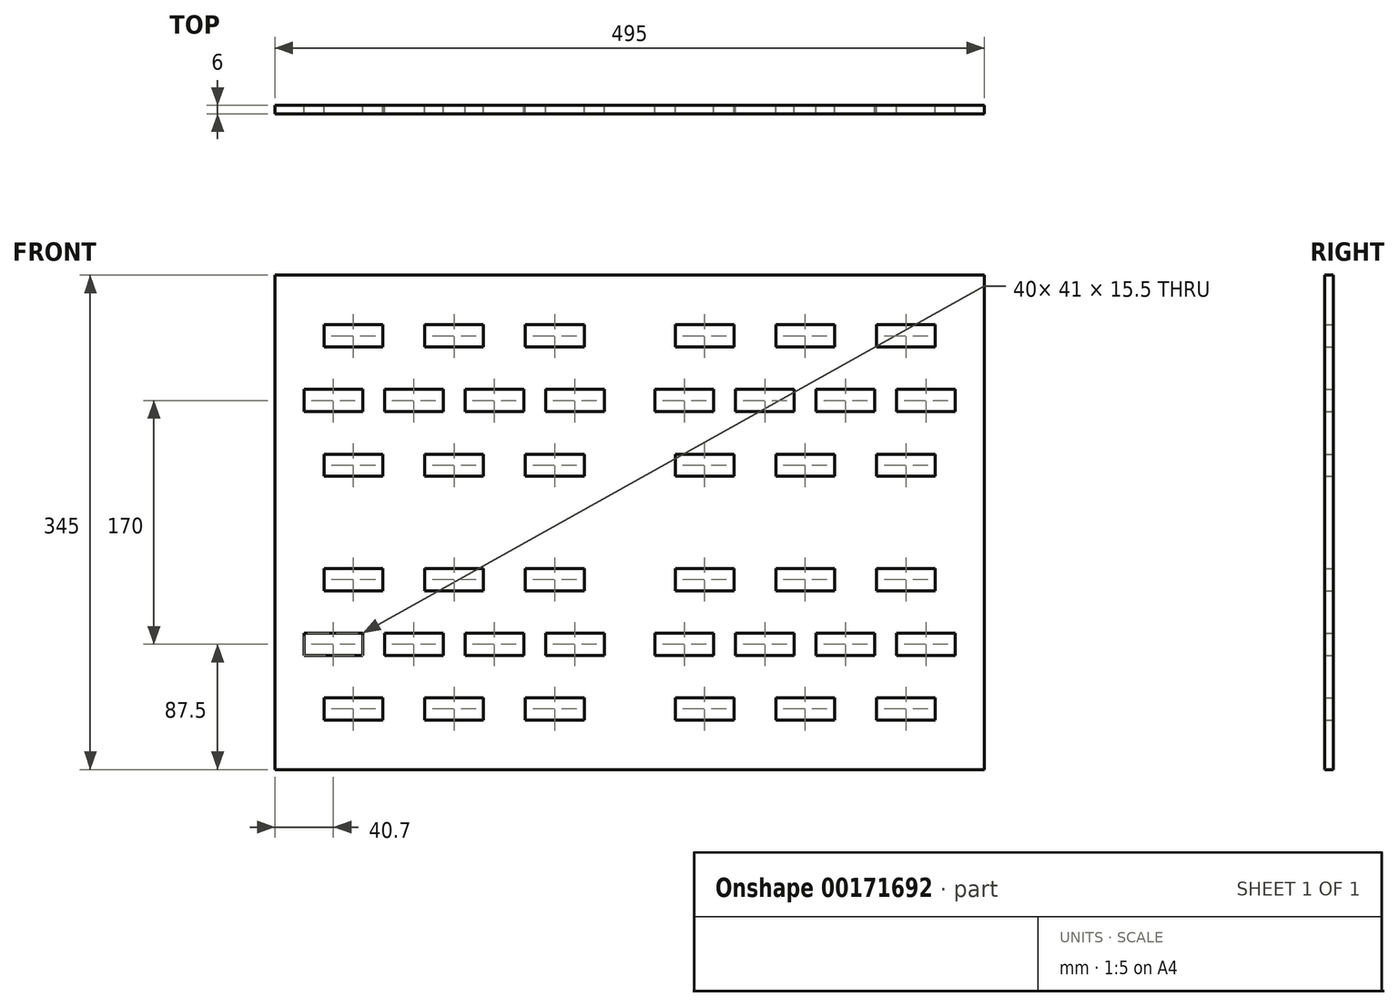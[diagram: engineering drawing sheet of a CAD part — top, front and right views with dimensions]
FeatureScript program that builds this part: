
annotation { "Feature Type Name" : "Feature", "Feature Type Description" : "" }
export const myFeature = defineFeature(function(context is Context, id is Id, definition is map)
    precondition{}
    {
        {
            var Q0;
            Q0=qCreatedBy(makeId("Front.planeOp"),FACE);
            var sketch = newSketch(context, id + "F0", { "sketchPlane" : qUnion([Q0])});
            skLineSegment(sketch, "E0.bottom", {"start": v(227.5, -172.5) * mm, "end": v(-227.5, -172.5) * mm});
            skLineSegment(sketch, "E0.top", {"start": v(226.92, 172.5) * mm, "end": v(-228.08, 172.5) * mm});
            skLineSegment(sketch, "E0.left", {"start": v(247.5, -152.5) * mm, "end": v(247.5, 152.5) * mm});
            skLineSegment(sketch, "E0.right", {"start": v(-247.5, -152.5) * mm, "end": v(-247.5, 152.5) * mm});
            skPoint(sketch, "E1.visualSharp", {"position": v(-247.5, 172.5) * mm});
            skPoint(sketch, "E2.visualSharp", {"position": v(247.5, 172.5) * mm});
            skPoint(sketch, "E3.visualSharp", {"position": v(247.5, -172.5) * mm});
            skPoint(sketch, "E4.visualSharp", {"position": v(-247.5, -172.5) * mm});
            skLineSegment(sketch, "E5", {"start": v(-247.5, 152.5) * mm, "end": v(-247.5, 172.5) * mm});
            skLineSegment(sketch, "E6", {"start": v(-247.5, 172.5) * mm, "end": v(-228.08, 172.5) * mm});
            skLineSegment(sketch, "E7", {"start": v(-247.5, -172.5) * mm, "end": v(-247.5, -152.5) * mm});
            skLineSegment(sketch, "E8", {"start": v(-247.5, -172.5) * mm, "end": v(-227.5, -172.5) * mm});
            skLineSegment(sketch, "E9", {"start": v(247.5, -152.5) * mm, "end": v(247.5, -172.5) * mm});
            skLineSegment(sketch, "E10", {"start": v(227.5, -172.5) * mm, "end": v(247.5, -172.5) * mm});
            skLineSegment(sketch, "E11", {"start": v(226.92, 172.5) * mm, "end": v(247.5, 172.5) * mm});
            skLineSegment(sketch, "E12", {"start": v(247.5, 152.5) * mm, "end": v(247.5, 172.5) * mm});
            skPoint(sketch, "E13.1.0.2", {"position": v(-2.5, 172.5) * mm});
            skLineSegment(sketch, "E14.bottom", {"start": v(-213.25, 137.88) * mm, "end": v(-172.25, 137.88) * mm});
            skLineSegment(sketch, "E14.top", {"start": v(-213.25, 122.38) * mm, "end": v(-172.25, 122.38) * mm});
            skLineSegment(sketch, "E14.left", {"start": v(-213.25, 137.88) * mm, "end": v(-213.25, 122.38) * mm});
            skLineSegment(sketch, "E14.right", {"start": v(-172.25, 137.88) * mm, "end": v(-172.25, 122.38) * mm});
            skLineSegment(sketch, "E15.0.1.0", {"start": v(-213.25, 47.62) * mm, "end": v(-172.25, 47.62) * mm});
            skLineSegment(sketch, "E15.0.1.1", {"start": v(-172.25, 47.62) * mm, "end": v(-172.25, 32.12) * mm});
            skLineSegment(sketch, "E15.0.1.2", {"start": v(-213.25, 47.62) * mm, "end": v(-213.25, 32.12) * mm});
            skLineSegment(sketch, "E15.0.1.3", {"start": v(-213.25, 32.12) * mm, "end": v(-172.25, 32.12) * mm});
            skLineSegment(sketch, "E15.1.0.0", {"start": v(-143, 137.88) * mm, "end": v(-102, 137.88) * mm});
            skLineSegment(sketch, "E15.1.0.1", {"start": v(-102, 137.88) * mm, "end": v(-102, 122.38) * mm});
            skLineSegment(sketch, "E15.1.0.2", {"start": v(-143, 137.88) * mm, "end": v(-143, 122.38) * mm});
            skLineSegment(sketch, "E15.1.0.3", {"start": v(-143, 122.38) * mm, "end": v(-102, 122.38) * mm});
            skLineSegment(sketch, "E15.1.1.0", {"start": v(-143, 47.62) * mm, "end": v(-102, 47.62) * mm});
            skLineSegment(sketch, "E15.1.1.1", {"start": v(-102, 47.62) * mm, "end": v(-102, 32.12) * mm});
            skLineSegment(sketch, "E15.1.1.2", {"start": v(-143, 47.62) * mm, "end": v(-143, 32.13) * mm});
            skLineSegment(sketch, "E15.1.1.3", {"start": v(-143, 32.12) * mm, "end": v(-102, 32.13) * mm});
            skLineSegment(sketch, "E15.2.0.0", {"start": v(-72.75, 137.88) * mm, "end": v(-31.75, 137.88) * mm});
            skLineSegment(sketch, "E15.2.0.1", {"start": v(-31.75, 137.88) * mm, "end": v(-31.75, 122.38) * mm});
            skLineSegment(sketch, "E15.2.0.2", {"start": v(-72.75, 137.88) * mm, "end": v(-72.75, 122.38) * mm});
            skLineSegment(sketch, "E15.2.0.3", {"start": v(-72.75, 122.38) * mm, "end": v(-31.75, 122.38) * mm});
            skLineSegment(sketch, "E15.2.1.0", {"start": v(-72.75, 47.62) * mm, "end": v(-31.75, 47.62) * mm});
            skLineSegment(sketch, "E15.2.1.1", {"start": v(-31.75, 47.62) * mm, "end": v(-31.75, 32.12) * mm});
            skLineSegment(sketch, "E15.2.1.2", {"start": v(-72.75, 47.62) * mm, "end": v(-72.75, 32.13) * mm});
            skLineSegment(sketch, "E15.2.1.3", {"start": v(-72.75, 32.12) * mm, "end": v(-31.75, 32.12) * mm});
            skLineSegment(sketch, "E15.direction1", {"start": v(-213.25, 122.38) * mm, "end": v(-143, 122.38) * mm, "construction": true});
            skLineSegment(sketch, "E15.direction2", {"start": v(-213.25, 122.38) * mm, "end": v(-213.25, 32.12) * mm, "construction": true});
            skLineSegment(sketch, "E16.bottom", {"start": v(-227.3, 92.75) * mm, "end": v(-186.3, 92.75) * mm});
            skLineSegment(sketch, "E16.top", {"start": v(-227.3, 77.25) * mm, "end": v(-186.3, 77.25) * mm});
            skLineSegment(sketch, "E16.left", {"start": v(-227.3, 92.75) * mm, "end": v(-227.3, 77.25) * mm});
            skLineSegment(sketch, "E16.right", {"start": v(-186.3, 92.75) * mm, "end": v(-186.3, 77.25) * mm});
            skLineSegment(sketch, "E17.1.0.0", {"start": v(-171.1, 92.75) * mm, "end": v(-171.1, 77.25) * mm});
            skLineSegment(sketch, "E17.1.0.1", {"start": v(-130.1, 92.75) * mm, "end": v(-130.1, 77.25) * mm});
            skLineSegment(sketch, "E17.1.0.2", {"start": v(-171.1, 77.25) * mm, "end": v(-130.1, 77.25) * mm});
            skLineSegment(sketch, "E17.1.0.3", {"start": v(-171.1, 92.75) * mm, "end": v(-130.1, 92.75) * mm});
            skLineSegment(sketch, "E17.2.0.0", {"start": v(-114.9, 92.75) * mm, "end": v(-114.9, 77.25) * mm});
            skLineSegment(sketch, "E17.2.0.1", {"start": v(-73.9, 92.75) * mm, "end": v(-73.9, 77.25) * mm});
            skLineSegment(sketch, "E17.2.0.2", {"start": v(-114.9, 77.25) * mm, "end": v(-73.9, 77.25) * mm});
            skLineSegment(sketch, "E17.2.0.3", {"start": v(-114.9, 92.75) * mm, "end": v(-73.9, 92.75) * mm});
            skLineSegment(sketch, "E17.3.0.0", {"start": v(-58.7, 92.75) * mm, "end": v(-58.7, 77.25) * mm});
            skLineSegment(sketch, "E17.3.0.1", {"start": v(-17.7, 92.75) * mm, "end": v(-17.7, 77.25) * mm});
            skLineSegment(sketch, "E17.3.0.2", {"start": v(-58.7, 77.25) * mm, "end": v(-17.7, 77.25) * mm});
            skLineSegment(sketch, "E17.3.0.3", {"start": v(-58.7, 92.75) * mm, "end": v(-17.7, 92.75) * mm});
            skLineSegment(sketch, "E17.direction1", {"start": v(-227.3, 77.25) * mm, "end": v(-171.1, 77.25) * mm, "construction": true});
            skLineSegment(sketch, "E18.direction1", {"start": v(-213.25, 32.12) * mm, "end": v(31.75, 32.12) * mm, "construction": true});
            skLineSegment(sketch, "E18.direction2", {"start": v(-213.25, 32.12) * mm, "end": v(-213.25, -137.87) * mm, "construction": true});
            skLineSegment(sketch, "E19.0.1.0", {"start": v(130.1, 92.75) * mm, "end": v(171.1, 92.75) * mm});
            skLineSegment(sketch, "E19.3.1.0", {"start": v(172.25, 122.38) * mm, "end": v(213.25, 122.38) * mm});
            skLineSegment(sketch, "E19.6.1.0", {"start": v(186.3, 77.25) * mm, "end": v(227.3, 77.25) * mm});
            skLineSegment(sketch, "E19.9.1.0", {"start": v(31.75, 32.12) * mm, "end": v(72.75, 32.12) * mm});
            skLineSegment(sketch, "E19.12.1.0", {"start": v(102, 32.12) * mm, "end": v(143, 32.12) * mm});
            skLineSegment(sketch, "E19.15.1.0", {"start": v(172.25, 137.88) * mm, "end": v(213.25, 137.88) * mm});
            skLineSegment(sketch, "E19.18.1.0", {"start": v(172.25, 32.12) * mm, "end": v(213.25, 32.12) * mm});
            skLineSegment(sketch, "E19.21.1.0", {"start": v(102, 122.38) * mm, "end": v(143, 122.38) * mm});
            skLineSegment(sketch, "E19.24.1.0", {"start": v(172.25, 47.62) * mm, "end": v(213.25, 47.62) * mm});
            skLineSegment(sketch, "E19.27.1.0", {"start": v(102, 137.88) * mm, "end": v(143, 137.88) * mm});
            skLineSegment(sketch, "E19.30.1.0", {"start": v(31.75, 122.38) * mm, "end": v(102, 122.38) * mm, "construction": true});
            skLineSegment(sketch, "E19.33.1.0", {"start": v(102, 47.62) * mm, "end": v(143, 47.62) * mm});
            skLineSegment(sketch, "E19.36.1.0", {"start": v(186.3, 92.75) * mm, "end": v(227.3, 92.75) * mm});
            skLineSegment(sketch, "E19.39.1.0", {"start": v(17.7, 92.75) * mm, "end": v(58.7, 92.75) * mm});
            skLineSegment(sketch, "E19.42.1.0", {"start": v(73.9, 92.75) * mm, "end": v(114.9, 92.75) * mm});
            skLineSegment(sketch, "E19.45.1.0", {"start": v(17.7, 77.25) * mm, "end": v(73.9, 77.25) * mm, "construction": true});
            skLineSegment(sketch, "E19.48.1.0", {"start": v(31.75, 122.38) * mm, "end": v(72.75, 122.38) * mm});
            skLineSegment(sketch, "E19.51.1.0", {"start": v(31.75, 122.38) * mm, "end": v(31.75, 32.13) * mm, "construction": true});
            skLineSegment(sketch, "E19.54.1.0", {"start": v(130.1, 77.25) * mm, "end": v(171.1, 77.25) * mm});
            skLineSegment(sketch, "E19.57.1.0", {"start": v(31.75, 47.62) * mm, "end": v(72.75, 47.62) * mm});
            skLineSegment(sketch, "E19.60.1.0", {"start": v(73.9, 77.25) * mm, "end": v(114.9, 77.25) * mm});
            skLineSegment(sketch, "E19.63.1.0", {"start": v(31.75, 137.88) * mm, "end": v(72.75, 137.88) * mm});
            skLineSegment(sketch, "E19.66.1.0", {"start": v(31.75, 137.88) * mm, "end": v(31.75, 122.38) * mm});
            skLineSegment(sketch, "E19.69.1.0", {"start": v(114.9, 92.75) * mm, "end": v(114.9, 77.25) * mm});
            skLineSegment(sketch, "E19.72.1.0", {"start": v(213.25, 47.63) * mm, "end": v(213.25, 32.13) * mm});
            skLineSegment(sketch, "E19.75.1.0", {"start": v(72.75, 137.88) * mm, "end": v(72.75, 122.38) * mm});
            skLineSegment(sketch, "E19.78.1.0", {"start": v(143, 137.88) * mm, "end": v(143, 122.38) * mm});
            skLineSegment(sketch, "E19.81.1.0", {"start": v(17.7, 77.25) * mm, "end": v(58.7, 77.25) * mm});
            skLineSegment(sketch, "E19.84.1.0", {"start": v(227.3, 92.75) * mm, "end": v(227.3, 77.25) * mm});
            skLineSegment(sketch, "E19.87.1.0", {"start": v(172.25, 47.63) * mm, "end": v(172.25, 32.13) * mm});
            skLineSegment(sketch, "E19.90.1.0", {"start": v(171.1, 92.75) * mm, "end": v(171.1, 77.25) * mm});
            skLineSegment(sketch, "E19.93.1.0", {"start": v(102, 137.88) * mm, "end": v(102, 122.38) * mm});
            skLineSegment(sketch, "E19.96.1.0", {"start": v(143, 47.63) * mm, "end": v(143, 32.13) * mm});
            skLineSegment(sketch, "E19.99.1.0", {"start": v(102, 47.63) * mm, "end": v(102, 32.13) * mm});
            skLineSegment(sketch, "E19.102.1.0", {"start": v(130.1, 92.75) * mm, "end": v(130.1, 77.25) * mm});
            skLineSegment(sketch, "E19.105.1.0", {"start": v(72.75, 47.63) * mm, "end": v(72.75, 32.13) * mm});
            skLineSegment(sketch, "E19.108.1.0", {"start": v(17.7, 92.75) * mm, "end": v(17.7, 77.25) * mm});
            skLineSegment(sketch, "E19.111.1.0", {"start": v(186.3, 92.75) * mm, "end": v(186.3, 77.25) * mm});
            skLineSegment(sketch, "E19.114.1.0", {"start": v(213.25, 137.88) * mm, "end": v(213.25, 122.38) * mm});
            skLineSegment(sketch, "E19.117.1.0", {"start": v(58.7, 92.75) * mm, "end": v(58.7, 77.25) * mm});
            skLineSegment(sketch, "E19.120.1.0", {"start": v(172.25, 137.88) * mm, "end": v(172.25, 122.38) * mm});
            skLineSegment(sketch, "E19.123.1.0", {"start": v(31.75, 47.63) * mm, "end": v(31.75, 32.13) * mm});
            skLineSegment(sketch, "E19.126.1.0", {"start": v(73.9, 92.75) * mm, "end": v(73.9, 77.25) * mm});
            skLineSegment(sketch, "E20.0.0.1", {"start": v(-114.9, -77.25) * mm, "end": v(-73.9, -77.25) * mm});
            skLineSegment(sketch, "E20.3.0.1", {"start": v(-72.75, -47.62) * mm, "end": v(-31.75, -47.62) * mm});
            skLineSegment(sketch, "E20.6.0.1", {"start": v(-58.7, -92.75) * mm, "end": v(-17.7, -92.75) * mm});
            skLineSegment(sketch, "E20.9.0.1", {"start": v(-213.25, -137.87) * mm, "end": v(-172.25, -137.87) * mm});
            skLineSegment(sketch, "E20.12.0.1", {"start": v(-143, -137.88) * mm, "end": v(-102, -137.87) * mm});
            skLineSegment(sketch, "E20.15.0.1", {"start": v(-72.75, -32.12) * mm, "end": v(-31.75, -32.12) * mm});
            skLineSegment(sketch, "E20.18.0.1", {"start": v(-72.75, -137.87) * mm, "end": v(-31.75, -137.87) * mm});
            skLineSegment(sketch, "E20.21.0.1", {"start": v(-143, -47.63) * mm, "end": v(-102, -47.62) * mm});
            skLineSegment(sketch, "E20.24.0.1", {"start": v(-72.75, -122.37) * mm, "end": v(-31.75, -122.37) * mm});
            skLineSegment(sketch, "E20.27.0.1", {"start": v(-143, -32.12) * mm, "end": v(-102, -32.12) * mm});
            skLineSegment(sketch, "E20.30.0.1", {"start": v(-213.25, -47.62) * mm, "end": v(-143, -47.62) * mm, "construction": true});
            skLineSegment(sketch, "E20.33.0.1", {"start": v(-143, -122.37) * mm, "end": v(-102, -122.37) * mm});
            skLineSegment(sketch, "E20.36.0.1", {"start": v(-58.7, -77.25) * mm, "end": v(-17.7, -77.25) * mm});
            skLineSegment(sketch, "E20.39.0.1", {"start": v(-227.3, -77.25) * mm, "end": v(-186.3, -77.25) * mm});
            skLineSegment(sketch, "E20.42.0.1", {"start": v(-171.1, -77.25) * mm, "end": v(-130.1, -77.25) * mm});
            skLineSegment(sketch, "E20.45.0.1", {"start": v(-227.3, -92.75) * mm, "end": v(-171.1, -92.75) * mm, "construction": true});
            skLineSegment(sketch, "E20.48.0.1", {"start": v(-213.25, -47.62) * mm, "end": v(-172.25, -47.62) * mm});
            skLineSegment(sketch, "E20.51.0.1", {"start": v(-213.25, -47.62) * mm, "end": v(-213.25, -137.87) * mm, "construction": true});
            skLineSegment(sketch, "E20.54.0.1", {"start": v(-114.9, -92.75) * mm, "end": v(-73.9, -92.75) * mm});
            skLineSegment(sketch, "E20.57.0.1", {"start": v(-213.25, -122.37) * mm, "end": v(-172.25, -122.37) * mm});
            skLineSegment(sketch, "E20.60.0.1", {"start": v(-171.1, -92.75) * mm, "end": v(-130.1, -92.75) * mm});
            skLineSegment(sketch, "E20.63.0.1", {"start": v(-213.25, -32.12) * mm, "end": v(-172.25, -32.12) * mm});
            skLineSegment(sketch, "E20.66.0.1", {"start": v(-213.25, -32.12) * mm, "end": v(-213.25, -47.62) * mm});
            skLineSegment(sketch, "E20.69.0.1", {"start": v(-130.1, -77.25) * mm, "end": v(-130.1, -92.75) * mm});
            skLineSegment(sketch, "E20.72.0.1", {"start": v(-31.75, -122.37) * mm, "end": v(-31.75, -137.87) * mm});
            skLineSegment(sketch, "E20.75.0.1", {"start": v(-172.25, -32.12) * mm, "end": v(-172.25, -47.62) * mm});
            skLineSegment(sketch, "E20.78.0.1", {"start": v(-102, -32.12) * mm, "end": v(-102, -47.62) * mm});
            skLineSegment(sketch, "E20.81.0.1", {"start": v(-227.3, -92.75) * mm, "end": v(-186.3, -92.75) * mm});
            skLineSegment(sketch, "E20.84.0.1", {"start": v(-17.7, -77.25) * mm, "end": v(-17.7, -92.75) * mm});
            skLineSegment(sketch, "E20.87.0.1", {"start": v(-72.75, -122.37) * mm, "end": v(-72.75, -137.87) * mm});
            skLineSegment(sketch, "E20.90.0.1", {"start": v(-73.9, -77.25) * mm, "end": v(-73.9, -92.75) * mm});
            skLineSegment(sketch, "E20.93.0.1", {"start": v(-143, -32.12) * mm, "end": v(-143, -47.62) * mm});
            skLineSegment(sketch, "E20.96.0.1", {"start": v(-102, -122.37) * mm, "end": v(-102, -137.87) * mm});
            skLineSegment(sketch, "E20.99.0.1", {"start": v(-143, -122.37) * mm, "end": v(-143, -137.87) * mm});
            skLineSegment(sketch, "E20.102.0.1", {"start": v(-114.9, -77.25) * mm, "end": v(-114.9, -92.75) * mm});
            skLineSegment(sketch, "E20.105.0.1", {"start": v(-172.25, -122.37) * mm, "end": v(-172.25, -137.87) * mm});
            skLineSegment(sketch, "E20.108.0.1", {"start": v(-227.3, -77.25) * mm, "end": v(-227.3, -92.75) * mm});
            skLineSegment(sketch, "E20.111.0.1", {"start": v(-58.7, -77.25) * mm, "end": v(-58.7, -92.75) * mm});
            skLineSegment(sketch, "E20.114.0.1", {"start": v(-31.75, -32.12) * mm, "end": v(-31.75, -47.62) * mm});
            skLineSegment(sketch, "E20.117.0.1", {"start": v(-186.3, -77.25) * mm, "end": v(-186.3, -92.75) * mm});
            skLineSegment(sketch, "E20.120.0.1", {"start": v(-72.75, -32.12) * mm, "end": v(-72.75, -47.62) * mm});
            skLineSegment(sketch, "E20.123.0.1", {"start": v(-213.25, -122.37) * mm, "end": v(-213.25, -137.87) * mm});
            skLineSegment(sketch, "E20.126.0.1", {"start": v(-171.1, -77.25) * mm, "end": v(-171.1, -92.75) * mm});
            skLineSegment(sketch, "E20.0.1.1", {"start": v(130.1, -77.25) * mm, "end": v(171.1, -77.25) * mm});
            skLineSegment(sketch, "E20.3.1.1", {"start": v(172.25, -47.62) * mm, "end": v(213.25, -47.62) * mm});
            skLineSegment(sketch, "E20.6.1.1", {"start": v(186.3, -92.75) * mm, "end": v(227.3, -92.75) * mm});
            skLineSegment(sketch, "E20.9.1.1", {"start": v(31.75, -137.87) * mm, "end": v(72.75, -137.87) * mm});
            skLineSegment(sketch, "E20.12.1.1", {"start": v(102, -137.88) * mm, "end": v(143, -137.87) * mm});
            skLineSegment(sketch, "E20.15.1.1", {"start": v(172.25, -32.12) * mm, "end": v(213.25, -32.12) * mm});
            skLineSegment(sketch, "E20.18.1.1", {"start": v(172.25, -137.87) * mm, "end": v(213.25, -137.87) * mm});
            skLineSegment(sketch, "E20.21.1.1", {"start": v(102, -47.63) * mm, "end": v(143, -47.62) * mm});
            skLineSegment(sketch, "E20.24.1.1", {"start": v(172.25, -122.37) * mm, "end": v(213.25, -122.37) * mm});
            skLineSegment(sketch, "E20.27.1.1", {"start": v(102, -32.12) * mm, "end": v(143, -32.12) * mm});
            skLineSegment(sketch, "E20.30.1.1", {"start": v(31.75, -47.62) * mm, "end": v(102, -47.62) * mm, "construction": true});
            skLineSegment(sketch, "E20.33.1.1", {"start": v(102, -122.37) * mm, "end": v(143, -122.37) * mm});
            skLineSegment(sketch, "E20.36.1.1", {"start": v(186.3, -77.25) * mm, "end": v(227.3, -77.25) * mm});
            skLineSegment(sketch, "E20.39.1.1", {"start": v(17.7, -77.25) * mm, "end": v(58.7, -77.25) * mm});
            skLineSegment(sketch, "E20.42.1.1", {"start": v(73.9, -77.25) * mm, "end": v(114.9, -77.25) * mm});
            skLineSegment(sketch, "E20.45.1.1", {"start": v(17.7, -92.75) * mm, "end": v(73.9, -92.75) * mm, "construction": true});
            skLineSegment(sketch, "E20.48.1.1", {"start": v(31.75, -47.62) * mm, "end": v(72.75, -47.62) * mm});
            skLineSegment(sketch, "E20.51.1.1", {"start": v(31.75, -47.62) * mm, "end": v(31.75, -137.87) * mm, "construction": true});
            skLineSegment(sketch, "E20.54.1.1", {"start": v(130.1, -92.75) * mm, "end": v(171.1, -92.75) * mm});
            skLineSegment(sketch, "E20.57.1.1", {"start": v(31.75, -122.37) * mm, "end": v(72.75, -122.37) * mm});
            skLineSegment(sketch, "E20.60.1.1", {"start": v(73.9, -92.75) * mm, "end": v(114.9, -92.75) * mm});
            skLineSegment(sketch, "E20.63.1.1", {"start": v(31.75, -32.12) * mm, "end": v(72.75, -32.12) * mm});
            skLineSegment(sketch, "E20.66.1.1", {"start": v(31.75, -32.12) * mm, "end": v(31.75, -47.62) * mm});
            skLineSegment(sketch, "E20.69.1.1", {"start": v(114.9, -77.25) * mm, "end": v(114.9, -92.75) * mm});
            skLineSegment(sketch, "E20.72.1.1", {"start": v(213.25, -122.37) * mm, "end": v(213.25, -137.87) * mm});
            skLineSegment(sketch, "E20.75.1.1", {"start": v(72.75, -32.12) * mm, "end": v(72.75, -47.62) * mm});
            skLineSegment(sketch, "E20.78.1.1", {"start": v(143, -32.12) * mm, "end": v(143, -47.62) * mm});
            skLineSegment(sketch, "E20.81.1.1", {"start": v(17.7, -92.75) * mm, "end": v(58.7, -92.75) * mm});
            skLineSegment(sketch, "E20.84.1.1", {"start": v(227.3, -77.25) * mm, "end": v(227.3, -92.75) * mm});
            skLineSegment(sketch, "E20.87.1.1", {"start": v(172.25, -122.37) * mm, "end": v(172.25, -137.87) * mm});
            skLineSegment(sketch, "E20.90.1.1", {"start": v(171.1, -77.25) * mm, "end": v(171.1, -92.75) * mm});
            skLineSegment(sketch, "E20.93.1.1", {"start": v(102, -32.12) * mm, "end": v(102, -47.62) * mm});
            skLineSegment(sketch, "E20.96.1.1", {"start": v(143, -122.37) * mm, "end": v(143, -137.87) * mm});
            skLineSegment(sketch, "E20.99.1.1", {"start": v(102, -122.37) * mm, "end": v(102, -137.87) * mm});
            skLineSegment(sketch, "E20.102.1.1", {"start": v(130.1, -77.25) * mm, "end": v(130.1, -92.75) * mm});
            skLineSegment(sketch, "E20.105.1.1", {"start": v(72.75, -122.37) * mm, "end": v(72.75, -137.87) * mm});
            skLineSegment(sketch, "E20.108.1.1", {"start": v(17.7, -77.25) * mm, "end": v(17.7, -92.75) * mm});
            skLineSegment(sketch, "E20.111.1.1", {"start": v(186.3, -77.25) * mm, "end": v(186.3, -92.75) * mm});
            skLineSegment(sketch, "E20.114.1.1", {"start": v(213.25, -32.12) * mm, "end": v(213.25, -47.62) * mm});
            skLineSegment(sketch, "E20.117.1.1", {"start": v(58.7, -77.25) * mm, "end": v(58.7, -92.75) * mm});
            skLineSegment(sketch, "E20.120.1.1", {"start": v(172.25, -32.12) * mm, "end": v(172.25, -47.62) * mm});
            skLineSegment(sketch, "E20.123.1.1", {"start": v(31.75, -122.37) * mm, "end": v(31.75, -137.87) * mm});
            skLineSegment(sketch, "E20.126.1.1", {"start": v(73.9, -77.25) * mm, "end": v(73.9, -92.75) * mm});
            skSolve(sketch);
        }
        {
            var Q0;
            Q0=qSketchRegion(id+"F0",true);
            extrude(context, id + "F1", {"entities" : qUnion([Q0]), "endBound" : BoundingType.SYMMETRIC, "depth" : 6 * mm, "offsetDistance" : 25 * mm});
        }
    });
